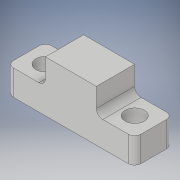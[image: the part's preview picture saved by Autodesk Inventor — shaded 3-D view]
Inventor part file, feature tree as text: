
AUTODESK INVENTOR PART (.ipt)
format: ipt  version: 2017 (Build 210142000, 142)  size: 126,976 bytes
history: native  units: in
note: dims shown in document units (in); Inventor stores cm internally (conversion verified against a paired STEP export)
features: extrude x2, sketch x2, fillet x1, mirror x1
ambient origin geometry x8: Origin, YZ Plane, XZ Plane, XY Plane, X Axis, Y Axis, Z Axis, Center Point
bodies: Solid1 (feature_tree)
feature tree (6):
  extrude  "Extrusion1"  Depth=1.0in
  fillet  "Fillet1"  Radius=0.5in
  extrude  "Extrusion2"  Depth=0.75in TaperAngle=0.0deg
  mirror  "Mirror1"
  sketch  "Sketch1"  dims[d0=1.25in d1=1.0in d2=0.5in]
  sketch  "Sketch2"  dims[d3=0.5in d4=0.75in d5=0.0in d6=0.125in d7=0.375in d8=0.5in d9=0.0in]
